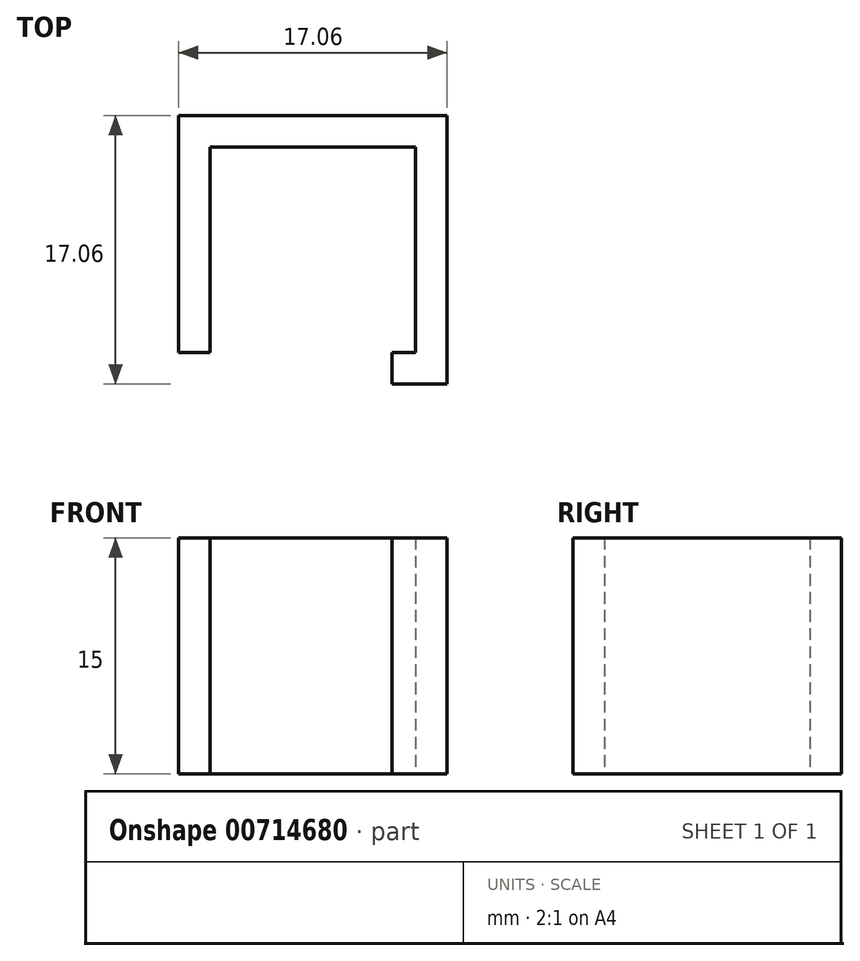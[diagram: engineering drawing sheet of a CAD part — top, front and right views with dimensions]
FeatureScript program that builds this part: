
annotation { "Feature Type Name" : "Feature", "Feature Type Description" : "" }
export const myFeature = defineFeature(function(context is Context, id is Id, definition is map)
    precondition{}
    {
        {
            var Q0;
            Q0=qCreatedBy(makeId("Top.planeOp"),FACE);
            var sketch = newSketch(context, id + "F0", { "sketchPlane" : qUnion([Q0])});
            skLineSegment(sketch, "E0.bottom", {"start": v(-6.52, 6.52) * mm, "end": v(6.53, 6.52) * mm});
            skLineSegment(sketch, "E0.top", {"start": v(-6.53, -6.53) * mm, "end": v(6.52, -6.53) * mm});
            skLineSegment(sketch, "E0.left", {"start": v(-6.52, 6.53) * mm, "end": v(-6.53, -6.52) * mm});
            skLineSegment(sketch, "E0.right", {"start": v(6.53, 6.53) * mm, "end": v(6.52, -6.53) * mm});
            skPoint(sketch, "E0.middle", {"position": v(0, 0) * mm});
            skLineSegment(sketch, "E1", {"start": v(-8.53, -6.53) * mm, "end": v(-8.53, 8.53) * mm});
            skLineSegment(sketch, "E2", {"start": v(-8.53, 8.53) * mm, "end": v(8.53, 8.53) * mm});
            skLineSegment(sketch, "E3", {"start": v(8.53, 8.53) * mm, "end": v(8.52, -8.53) * mm});
            skLineSegment(sketch, "E4", {"start": v(8.52, -8.53) * mm, "end": v(5.02, -8.53) * mm});
            skLineSegment(sketch, "E5", {"start": v(5.02, -8.53) * mm, "end": v(5.02, -6.53) * mm});
            skLineSegment(sketch, "E6", {"start": v(-6.53, -6.53) * mm, "end": v(-8.53, -6.53) * mm});
            skSolve(sketch);
        }
        {
            var Q0;
            Q0=makeQuery(id+"F0.imprint","IMPRINT",FACE,{"disambiguationData":[TD([[makeQuery(id+"F0.imprint","IMPRINT",EDGE,{"derivedFrom":sQuery(id+"F0.wireOp",EDGE,"E0.bottom")}),1.0]])]});
            extrude(context, id + "F1", {"entities" : qUnion([Q0]), "endBound" : BoundingType.SYMMETRIC, "depth" : 15 * mm, "offsetDistance" : 25 * mm});
        }
    });
